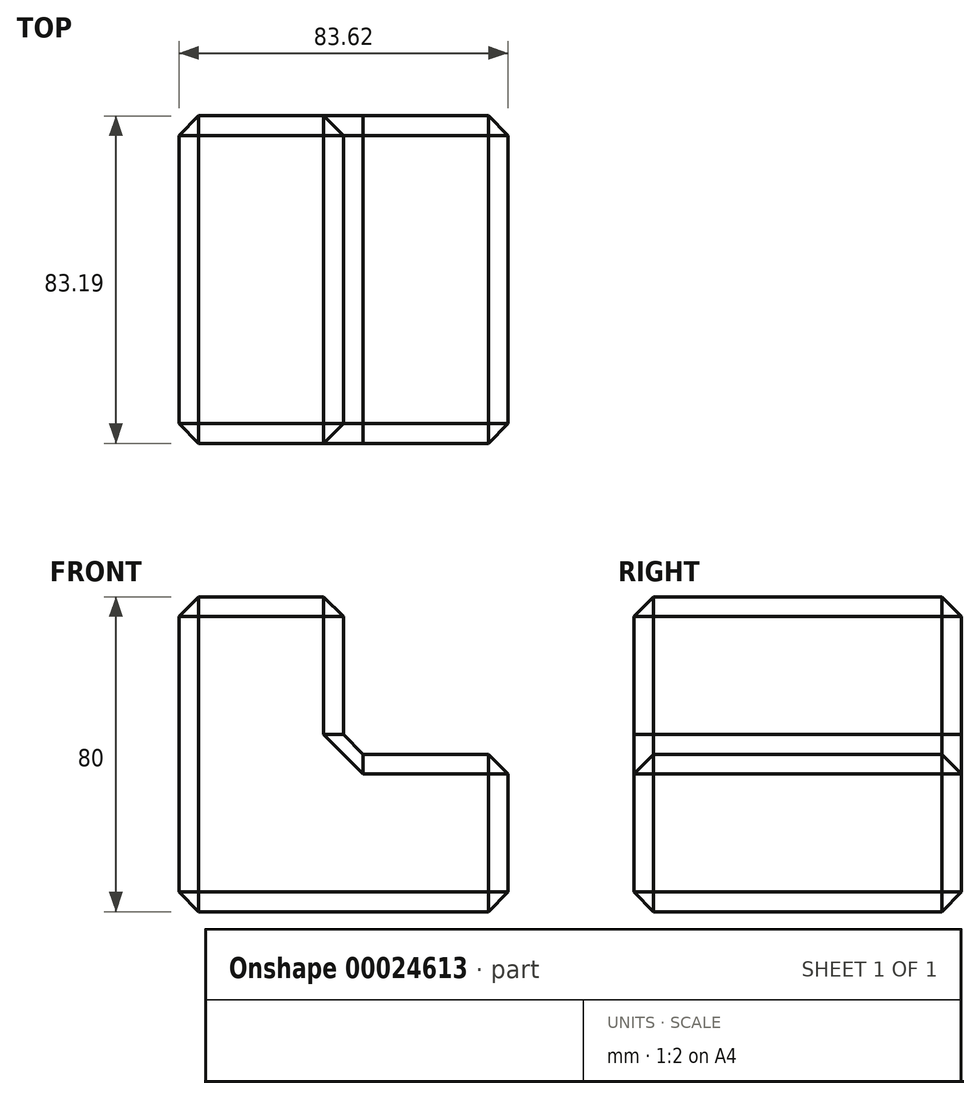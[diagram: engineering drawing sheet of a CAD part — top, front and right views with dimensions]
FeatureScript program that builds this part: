
annotation { "Feature Type Name" : "Feature", "Feature Type Description" : "" }
export const myFeature = defineFeature(function(context is Context, id is Id, definition is map)
    precondition{}
    {
        {
            var Q0;
            Q0=qCreatedBy(makeId("Top.planeOp"),FACE);
            var sketch = newSketch(context, id + "F0", { "sketchPlane" : qUnion([Q0])});
            skLineSegment(sketch, "E0.bottom", {"start": v(-59.13, -45.93) * mm, "end": v(24.5, -45.93) * mm});
            skLineSegment(sketch, "E0.top", {"start": v(-59.13, 37.26) * mm, "end": v(24.5, 37.26) * mm});
            skLineSegment(sketch, "E0.left", {"start": v(-59.13, -45.93) * mm, "end": v(-59.13, 37.26) * mm});
            skLineSegment(sketch, "E0.right", {"start": v(24.5, -45.93) * mm, "end": v(24.5, 37.26) * mm});
            skSolve(sketch);
        }
        {
            var Q0;
            Q0=makeQuery(id+"F0.imprint","IMPRINT",FACE,{"disambiguationData":[TD([[makeQuery(id+"F0.imprint","IMPRINT",EDGE,{"derivedFrom":sQuery(id+"F0.wireOp",EDGE,"E0.bottom")}),1.0]])]});
            extrude(context, id + "F1", {"entities" : qUnion([Q0]), "depth" : 40 * mm});
        }
        {
            var Q0;
            Q0=makeQuery(id+"F1.opExtrude","CAP_FACE",FACE,{"disambiguationData":[OSD([sQuery(id+"F0.wireOp",EDGE,"E0.bottom"),sQuery(id+"F0.wireOp",EDGE,"E0.top"),sQuery(id+"F0.wireOp",EDGE,"E0.left"),sQuery(id+"F0.wireOp",EDGE,"E0.right")])],"isStart":false});
            var sketch = newSketch(context, id + "F2", { "sketchPlane" : qUnion([Q0])});
            skLineSegment(sketch, "E1", {"start": v(-17.32, 37.26) * mm, "end": v(-17.32, -45.93) * mm});
            skSolve(sketch);
        }
        {
            var Q0;
            {var subQ1=sQuery(id+"F2.wireOp",EDGE,"E1");Q0=makeQuery(id+"F2.imprint","IMPRINT",FACE,{"disambiguationData":[TD([[makeQuery(id+"F2.imprint","IMPRINT",EDGE,{"derivedFrom":subQ1}),-1.0]])]});}
            extrude(context, id + "F3", {"entities" : qUnion([Q0]), "operationType" : NewBodyOperationType.ADD, "depth" : 40 * mm});
        }
        {
            var Q0;
            Q0=makeQuery(id+"F3.opExtrude","CAP_EDGE",EDGE,{"disambiguationData":[OSD([sQuery(id+"F2.wireOp",EDGE,"E1")])],"isStart":false});
            var Q1;
            Q1=makeQuery(id+"F3.opExtrude","CAP_FACE",FACE,{"disambiguationData":[OSD([sQuery(id+"F0.wireOp",EDGE,"E0.bottom"),sQuery(id+"F0.wireOp",EDGE,"E0.top"),sQuery(id+"F0.wireOp",EDGE,"E0.left"),sQuery(id+"F2.wireOp",EDGE,"E1")])],"isStart":false});
            var Q2;
            Q2=makeQuery(id+"F3.opExtrude","SWEPT_EDGE",EDGE,{"disambiguationData":[OSD([sQuery(id+"F0.wireOp",EDGE,"E0.bottom"),sQuery(id+"F2.wireOp",EDGE,"E1")])]});
            var Q3;
            {var subQ0=sQuery(id+"F0.wireOp",EDGE,"E0.bottom");Q3=makeQuery(id+"F3.boolean.opBoolean","MERGE",FACE,{"derivedFrom":[makeQuery(id+"F1.opExtrude","SWEPT_FACE",FACE,{"disambiguationData":[OSD([subQ0])]}),makeQuery(id+"F3.opExtrude","SWEPT_FACE",FACE,{"disambiguationData":[OSD([subQ0])]})]});}
            var Q4;
            Q4=makeQuery(id+"F1.opExtrude","CAP_FACE",FACE,{"disambiguationData":[OSD([sQuery(id+"F0.wireOp",EDGE,"E0.bottom"),sQuery(id+"F0.wireOp",EDGE,"E0.top"),sQuery(id+"F0.wireOp",EDGE,"E0.left"),sQuery(id+"F0.wireOp",EDGE,"E0.right")])],"isStart":false});
            var Q5;
            Q5=makeQuery(id+"F3.opExtrude","SWEPT_FACE",FACE,{"disambiguationData":[OSD([sQuery(id+"F2.wireOp",EDGE,"E1")])]});
            var Q6;
            Q6=makeQuery(id+"F1.opExtrude","SWEPT_FACE",FACE,{"disambiguationData":[OSD([sQuery(id+"F0.wireOp",EDGE,"E0.right")])]});
            var Q7;
            {var subQ0=sQuery(id+"F0.wireOp",EDGE,"E0.top");Q7=makeQuery(id+"F3.boolean.opBoolean","MERGE",FACE,{"derivedFrom":[makeQuery(id+"F1.opExtrude","SWEPT_FACE",FACE,{"disambiguationData":[OSD([subQ0])]}),makeQuery(id+"F3.opExtrude","SWEPT_FACE",FACE,{"disambiguationData":[OSD([subQ0])]})]});}
            var Q8;
            Q8=makeQuery(id+"F1.opExtrude","CAP_FACE",FACE,{"disambiguationData":[OSD([sQuery(id+"F0.wireOp",EDGE,"E0.bottom"),sQuery(id+"F0.wireOp",EDGE,"E0.top"),sQuery(id+"F0.wireOp",EDGE,"E0.left"),sQuery(id+"F0.wireOp",EDGE,"E0.right")])],"isStart":true});
            var Q9;
            {var subQ0=sQuery(id+"F0.wireOp",EDGE,"E0.left");Q9=makeQuery(id+"F3.boolean.opBoolean","MERGE",FACE,{"derivedFrom":[makeQuery(id+"F1.opExtrude","SWEPT_FACE",FACE,{"disambiguationData":[OSD([subQ0])]}),makeQuery(id+"F3.opExtrude","SWEPT_FACE",FACE,{"disambiguationData":[OSD([subQ0])]})]});}
            chamfer(context, id + "F4", {"entities" : qUnion([Q0, Q1, Q2, Q3, Q4, Q5, Q6, Q7, Q8, Q9]), "width" : 5 * mm, "tangentPropagation" : true});
        }
    });
